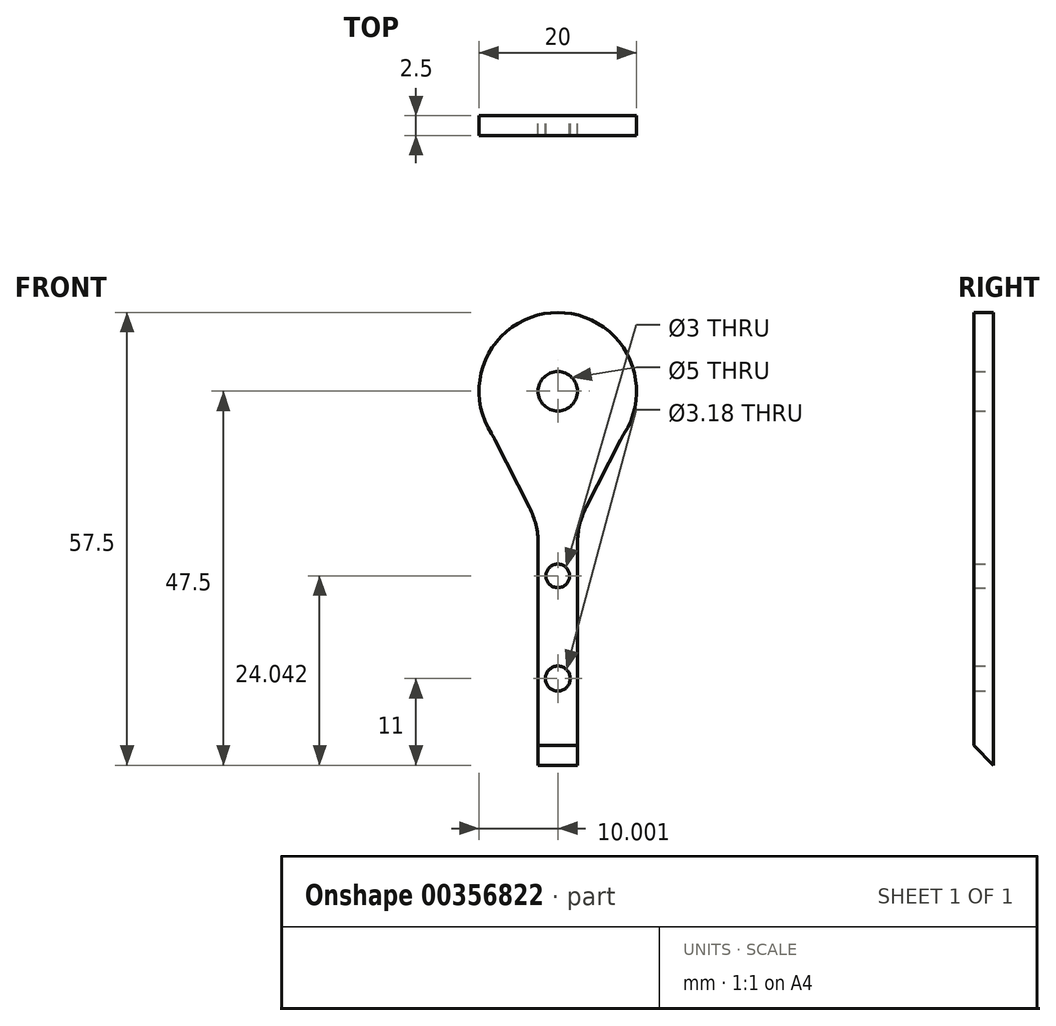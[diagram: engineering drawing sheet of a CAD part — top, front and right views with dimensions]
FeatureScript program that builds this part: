
annotation { "Feature Type Name" : "Feature", "Feature Type Description" : "" }
export const myFeature = defineFeature(function(context is Context, id is Id, definition is map)
    precondition{}
    {
        {
            var Q0;
            Q0=qCreatedBy(makeId("Front.planeOp"),FACE);
            var sketch = newSketch(context, id + "F0", { "sketchPlane" : qUnion([Q0])});
            skPoint(sketch, "E0.middle", {"position": v(-2.52, 0) * mm});
            skArc(sketch, "E1", {"start": v(5.7, 24.3) * mm, "mid": v(-2.52, 40) * mm, "end": v(-10.73, 24.3) * mm});
            skPoint(sketch, "E2.start.orphan", {"position": v(-12.52, 30) * mm});
            skLineSegment(sketch, "E3.trimOffspring", {"start": v(-0.02, 13.08) * mm, "end": v(-0.02, -20) * mm});
            skLineSegment(sketch, "E4", {"start": v(5.7, 24.3) * mm, "end": v(-0.02, 13.08) * mm});
            skLineSegment(sketch, "E5", {"start": v(-10.73, 24.3) * mm, "end": v(-5.02, 13.08) * mm});
            skLineSegment(sketch, "E6.trimOffspring", {"start": v(-5.02, 13.08) * mm, "end": v(-5.02, -20) * mm});
            skCircle(sketch, "E7", {"center": v(-2.52, 30) * mm, "radius": 2.5 * mm});
            skPoint(sketch, "E8.orphan", {"position": v(-5.02, 30) * mm});
            skPoint(sketch, "E0.bottom.start.orphan", {"position": v(-0.02, 30) * mm});
            skLineSegment(sketch, "E9", {"start": v(-5.02, -20) * mm, "end": v(-0.02, -20) * mm});
            skCircle(sketch, "E10", {"center": v(-2.52, -6.5) * mm, "radius": 1.5 * mm});
            skCircle(sketch, "E11", {"center": v(-2.52, 6.54) * mm, "radius": 1.5 * mm});
            skPoint(sketch, "E12.start.orphan", {"position": v(-2.52, -20) * mm});
            skPoint(sketch, "E13.start.orphan", {"position": v(-2.52, 13.08) * mm});
            skCircle(sketch, "E14", {"center": v(-2.52, -6.5) * mm, "radius": 1.59 * mm});
            skSolve(sketch);
        }
        {
            var Q0;
            Q0=makeQuery(id+"F0.imprint","IMPRINT",FACE,{"disambiguationData":[TD([[makeQuery(id+"F0.imprint","IMPRINT",EDGE,{"derivedFrom":sQuery(id+"F0.wireOp",EDGE,"E1")}),1.0]])]});
            extrude(context, id + "F1", {"entities" : qUnion([Q0]), "depth" : 2.5 * mm});
        }
        {
            var Q0;
            Q0=makeQuery(id+"F1.opExtrude","CAP_EDGE",EDGE,{"disambiguationData":[OSD([sQuery(id+"F0.wireOp",EDGE,"E9")])],"isStart":false});
            chamfer(context, id + "F2", {"entities" : qUnion([Q0]), "width" : 5 * mm, "tangentPropagation" : true});
        }
        {
            var Q0;
            Q0=makeQuery(id+"F1.opExtrude","SWEPT_EDGE",EDGE,{"disambiguationData":[OSD([sQuery(id+"F0.wireOp",EDGE,"E3.trimOffspring"),sQuery(id+"F0.wireOp",EDGE,"E4")])]});
            var Q1;
            Q1=makeQuery(id+"F1.opExtrude","SWEPT_EDGE",EDGE,{"disambiguationData":[OSD([sQuery(id+"F0.wireOp",EDGE,"E5"),sQuery(id+"F0.wireOp",EDGE,"E6.trimOffspring")])]});
            var Q2;
            Q2=makeQuery(id+"F1.opExtrude","SWEPT_EDGE",EDGE,{"disambiguationData":[OSD([sQuery(id+"F0.wireOp",EDGE,"E1"),sQuery(id+"F0.wireOp",EDGE,"E4")])]});
            var Q3;
            Q3=makeQuery(id+"F1.opExtrude","SWEPT_EDGE",EDGE,{"disambiguationData":[OSD([sQuery(id+"F0.wireOp",EDGE,"E1"),sQuery(id+"F0.wireOp",EDGE,"E5")])]});
            fillet(context, id + "F3", {"entities" : qUnion([Q0, Q1, Q2, Q3]), "radius" : 10 * mm, "tangentPropagation" : true, "allowEdgeOverflow" : false});
        }
    });
